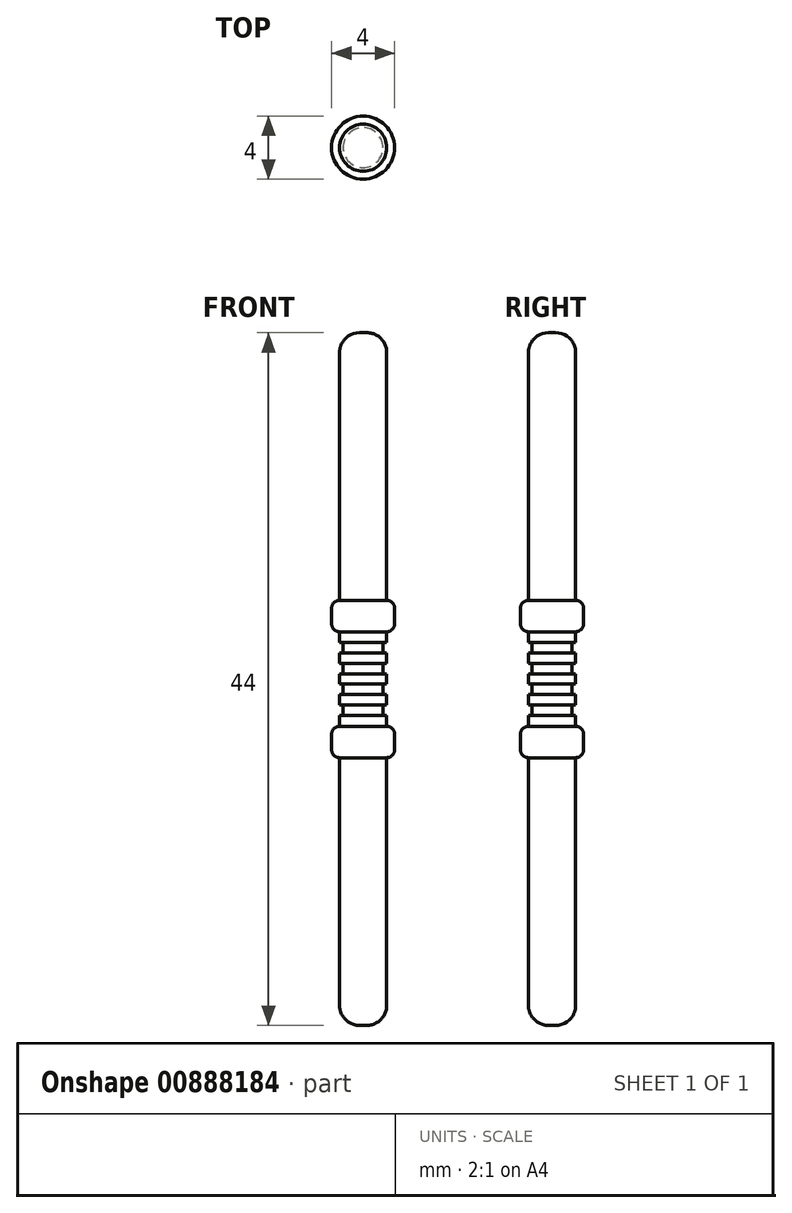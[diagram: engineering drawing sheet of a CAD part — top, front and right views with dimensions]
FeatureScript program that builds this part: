
annotation { "Feature Type Name" : "Feature", "Feature Type Description" : "" }
export const myFeature = defineFeature(function(context is Context, id is Id, definition is map)
    precondition{}
    {
        {
            var Q0;
            Q0=qCreatedBy(makeId("Top.planeOp"),FACE);
            var sketch = newSketch(context, id + "F0", { "sketchPlane" : qUnion([Q0])});
            skCircle(sketch, "E0", {"center": v(0, 0) * mm, "radius": 1.5 * mm});
            skSolve(sketch);
        }
        {
            var Q0;
            Q0 = qSketchRegion(id + "F0", true);
            extrude(context, id + "F1", {"entities" : qUnion([Q0]), "endBound" : BoundingType.SYMMETRIC, "depth" : 6 * mm, "offsetDistance" : 25.4 * mm});
        }
        {
            var Q0;
            Q0=makeQuery(id+"F1.opExtrude","CAP_FACE",FACE,{"disambiguationData":[OSD([sQuery(id+"F0.wireOp",EDGE,"E0")])],"isStart":false});
            var sketch = newSketch(context, id + "F2", { "sketchPlane" : qUnion([Q0])});
            skCircle(sketch, "E1", {"center": v(0, 0) * mm, "radius": 2 * mm});
            skSolve(sketch);
        }
        {
            var Q0;
            Q0 = qSketchRegion(id + "F2", true);
            extrude(context, id + "F3", {"entities" : qUnion([Q0]), "operationType" : NewBodyOperationType.ADD, "depth" : 2 * mm, "offsetDistance" : 25.4 * mm});
        }
        {
            var Q0;
            Q0=makeQuery(id+"F3.opExtrude","CAP_FACE",FACE,{"disambiguationData":[OSD([sQuery(id+"F2.wireOp",EDGE,"E1")])],"isStart":false});
            var sketch = newSketch(context, id + "F4", { "sketchPlane" : qUnion([Q0])});
            skCircle(sketch, "E2", {"center": v(0, 0) * mm, "radius": 1.5 * mm});
            skSolve(sketch);
        }
        {
            var Q0;
            Q0 = qSketchRegion(id + "F4", true);
            extrude(context, id + "F5", {"entities" : qUnion([Q0]), "operationType" : NewBodyOperationType.ADD, "depth" : 17 * mm, "offsetDistance" : 25.4 * mm});
        }
        {
            var Q0;
            Q0=makeQuery(id+"F5.opExtrude","CAP_EDGE",EDGE,{"disambiguationData":[OSD([sQuery(id+"F4.wireOp",EDGE,"E2")])],"isStart":false});
            fillet(context, id + "F6", {"entities" : qUnion([Q0]), "radius" : 1.27 * mm, "tangentPropagation" : true, "allowEdgeOverflow" : false});
        }
        {
            var Q0;
            Q0=makeQuery(id+"F1.opExtrude","SWEPT_BODY",BODY,{"disambiguationData":[OSD([sQuery(id+"F0.wireOp",EDGE,"E0")])]});
            var Q1;
            Q1=qCreatedBy(makeId("Top.planeOp"),FACE);
            mirror(context, id + "F7", {"operationType" : NewBodyOperationType.ADD, "entities" : qUnion([Q0]), "mirrorPlane" : qUnion([Q1])});
        }
        {
            var Q0;
            Q0=qCreatedBy(makeId("Front.planeOp"),FACE);
            var sketch = newSketch(context, id + "F8", { "sketchPlane" : qUnion([Q0])});
            skLineSegment(sketch, "E3.bottom", {"start": v(1.27, 2.32) * mm, "end": v(1.78, 2.32) * mm});
            skLineSegment(sketch, "E3.top", {"start": v(1.27, 1.65) * mm, "end": v(1.78, 1.65) * mm});
            skLineSegment(sketch, "E3.left", {"start": v(1.27, 2.32) * mm, "end": v(1.27, 1.65) * mm});
            skLineSegment(sketch, "E3.right", {"start": v(1.78, 2.32) * mm, "end": v(1.78, 1.65) * mm});
            skLineSegment(sketch, "E4.bottom", {"start": v(1.27, 1) * mm, "end": v(1.78, 1) * mm});
            skLineSegment(sketch, "E4.top", {"start": v(1.27, 0.33) * mm, "end": v(1.78, 0.33) * mm});
            skLineSegment(sketch, "E4.left", {"start": v(1.27, 1) * mm, "end": v(1.27, 0.33) * mm});
            skLineSegment(sketch, "E4.right", {"start": v(1.78, 1) * mm, "end": v(1.78, 0.33) * mm});
            skLineSegment(sketch, "E5.bottom", {"start": v(1.27, -0.33) * mm, "end": v(1.78, -0.33) * mm});
            skLineSegment(sketch, "E5.top", {"start": v(1.27, -1) * mm, "end": v(1.78, -1) * mm});
            skLineSegment(sketch, "E5.left", {"start": v(1.27, -0.33) * mm, "end": v(1.27, -1) * mm});
            skLineSegment(sketch, "E5.right", {"start": v(1.78, -0.33) * mm, "end": v(1.78, -1) * mm});
            skLineSegment(sketch, "E6.bottom", {"start": v(1.27, -1.65) * mm, "end": v(1.78, -1.65) * mm});
            skLineSegment(sketch, "E6.top", {"start": v(1.27, -2.32) * mm, "end": v(1.78, -2.32) * mm});
            skLineSegment(sketch, "E6.left", {"start": v(1.27, -1.65) * mm, "end": v(1.27, -2.32) * mm});
            skLineSegment(sketch, "E6.right", {"start": v(1.78, -1.65) * mm, "end": v(1.78, -2.32) * mm});
            skLineSegment(sketch, "E7", {"start": v(1.27, 1.65) * mm, "end": v(1.27, 1) * mm, "construction": true});
            skLineSegment(sketch, "E8", {"start": v(1.27, 0.33) * mm, "end": v(1.27, -0.33) * mm, "construction": true});
            skLineSegment(sketch, "E9", {"start": v(1.27, -1) * mm, "end": v(1.27, -1.65) * mm, "construction": true});
            skLineSegment(sketch, "E10", {"start": v(1.27, 0) * mm, "end": v(0, 0) * mm, "construction": true});
            skLineSegment(sketch, "E11", {"start": v(0, 0) * mm, "end": v(0, 1.26) * mm, "construction": true});
            skSolve(sketch);
        }
        {
            var Q0;
            Q0 = qSketchRegion(id + "F8", true);
            var Q1;
            Q1=sQuery(id+"F8.wireOp",EDGE,"E11");
            revolve(context, id + "F9", {"operationType" : NewBodyOperationType.REMOVE, "surfaceOperationType" : NewSurfaceOperationType.NEW, "entities" : qUnion([Q0]), "axis" : qUnion([Q1]), "revolveType" : RevolveType.FULL, "oppositeDirection" : true});
        }
        {
            var Q0;
            Q0=makeQuery(id+"F3.opExtrude","CAP_EDGE",EDGE,{"disambiguationData":[OSD([sQuery(id+"F2.wireOp",EDGE,"E1")])],"isStart":false});
            var Q1;
            Q1=makeQuery(id+"F3.opExtrude","CAP_EDGE",EDGE,{"disambiguationData":[OSD([sQuery(id+"F2.wireOp",EDGE,"E1")])],"isStart":true});
            var Q2;
            Q2=makeQuery(id+"F7.opPattern","COPY",EDGE,{"derivedFrom":makeQuery(id+"F3.opExtrude","CAP_EDGE",EDGE,{"disambiguationData":[OSD([sQuery(id+"F2.wireOp",EDGE,"E1")])],"isStart":true}),"instanceName":"1"});
            var Q3;
            Q3=makeQuery(id+"F7.opPattern","COPY",EDGE,{"derivedFrom":makeQuery(id+"F3.opExtrude","CAP_EDGE",EDGE,{"disambiguationData":[OSD([sQuery(id+"F2.wireOp",EDGE,"E1")])],"isStart":false}),"instanceName":"1"});
            fillet(context, id + "F10", {"entities" : qUnion([Q0, Q1, Q2, Q3]), "radius" : 0.5 * mm, "tangentPropagation" : true, "allowEdgeOverflow" : false});
        }
    });
